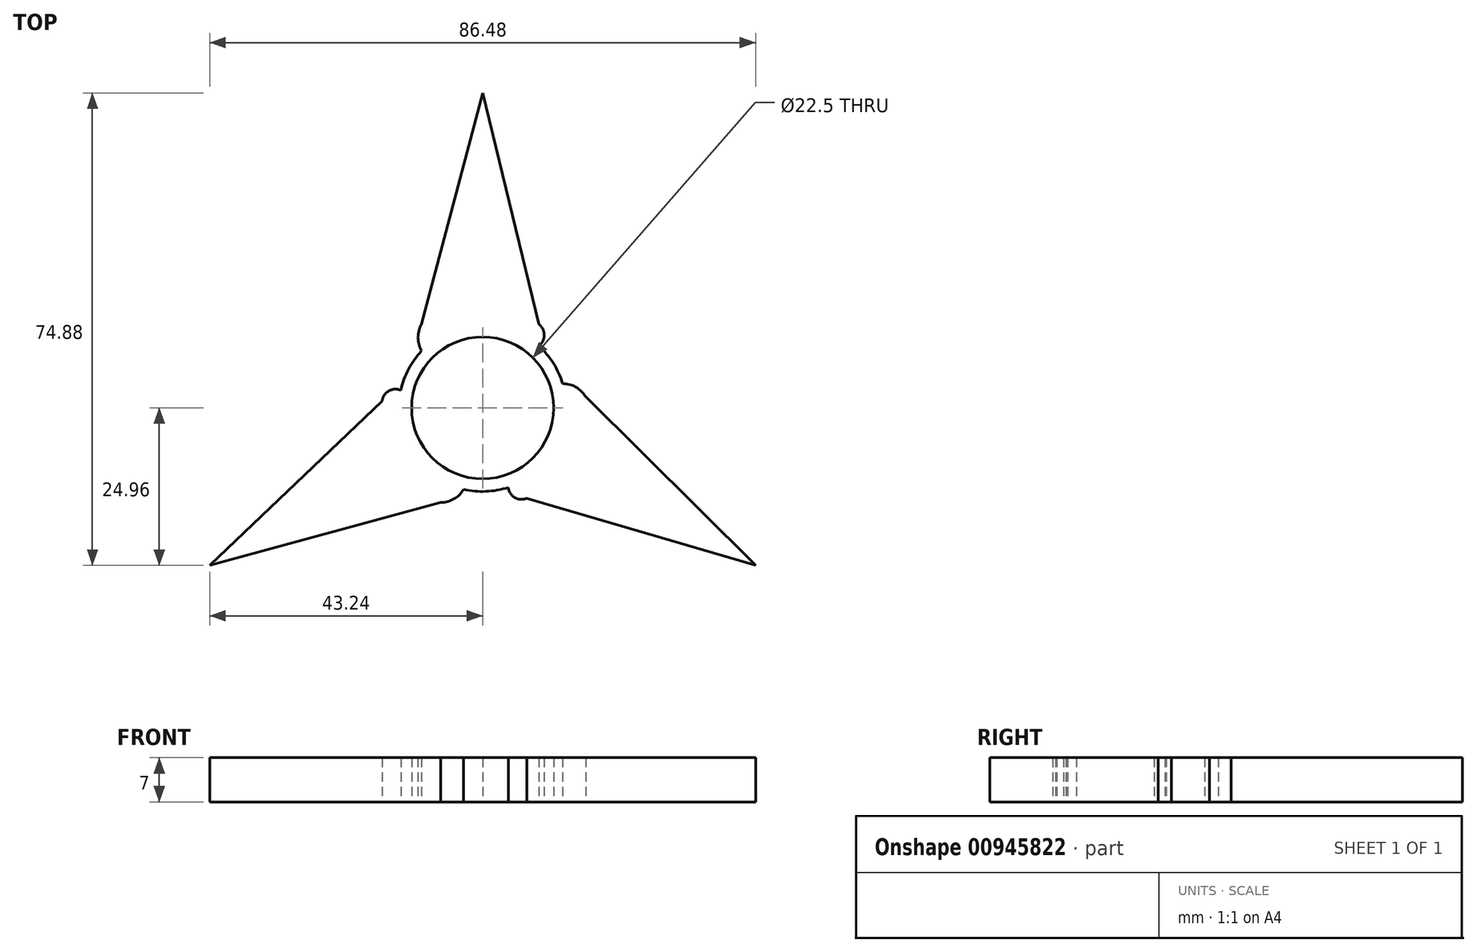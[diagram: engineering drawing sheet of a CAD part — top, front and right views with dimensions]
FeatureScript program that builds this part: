
annotation { "Feature Type Name" : "Feature", "Feature Type Description" : "" }
export const myFeature = defineFeature(function(context is Context, id is Id, definition is map)
    precondition{}
    {
        {
            var Q0;
            Q0=qCreatedBy(makeId("Top.planeOp"),FACE);
            var sketch = newSketch(context, id + "F0", { "sketchPlane" : qUnion([Q0])});
            skCircle(sketch, "E0", {"center": v(0, 0) * mm, "radius": 11.25 * mm});
            skCircle(sketch, "E1.0", {"center": v(0, 0) * mm, "radius": 13.25 * mm});
            skLineSegment(sketch, "E2", {"start": v(-9.67, 13.25) * mm, "end": v(8.89, 13.25) * mm});
            skLineSegment(sketch, "E3", {"start": v(8.89, 13.25) * mm, "end": v(0, 49.92) * mm});
            skLineSegment(sketch, "E4", {"start": v(0, 49.92) * mm, "end": v(-9.67, 13.25) * mm});
            skLineSegment(sketch, "E5.1.2", {"start": v(-15.92, 1.07) * mm, "end": v(-43.24, -24.96) * mm});
            skLineSegment(sketch, "E5.1.3", {"start": v(-6.64, -15) * mm, "end": v(-15.92, 1.07) * mm});
            skLineSegment(sketch, "E5.1.4", {"start": v(-43.24, -24.96) * mm, "end": v(-6.64, -15) * mm});
            skLineSegment(sketch, "E5.2.2", {"start": v(7.03, -14.32) * mm, "end": v(43.24, -24.96) * mm});
            skLineSegment(sketch, "E5.2.3", {"start": v(16.3, 1.75) * mm, "end": v(7.03, -14.32) * mm});
            skLineSegment(sketch, "E5.2.4", {"start": v(43.24, -24.96) * mm, "end": v(16.3, 1.75) * mm});
            skArc(sketch, "E6", {"start": v(-9.67, 13.25) * mm, "mid": v(-10.24, 11.16) * mm, "end": v(-9.67, 9.06) * mm});
            skArc(sketch, "E7", {"start": v(8.89, 9.83) * mm, "mid": v(9.76, 11.54) * mm, "end": v(8.89, 13.25) * mm});
            skArc(sketch, "E8.1.0", {"start": v(-12.95, 2.78) * mm, "mid": v(-14.87, 2.69) * mm, "end": v(-15.92, 1.07) * mm});
            skArc(sketch, "E8.1.1", {"start": v(-6.64, -15) * mm, "mid": v(-4.54, -14.44) * mm, "end": v(-3.01, -12.9) * mm});
            skArc(sketch, "E8.2.0", {"start": v(4.07, -12.61) * mm, "mid": v(5.11, -14.22) * mm, "end": v(7.03, -14.32) * mm});
            skArc(sketch, "E8.2.1", {"start": v(16.3, 1.75) * mm, "mid": v(14.78, 3.29) * mm, "end": v(12.68, 3.84) * mm});
            skSolve(sketch);
        }
        {
            var Q0;
            Q0 = qSketchRegion(id + "F0", true);
            extrude(context, id + "F1", {"entities" : qUnion([Q0]), "depth" : 7 * mm, "offsetDistance" : 25 * mm});
        }
    });
